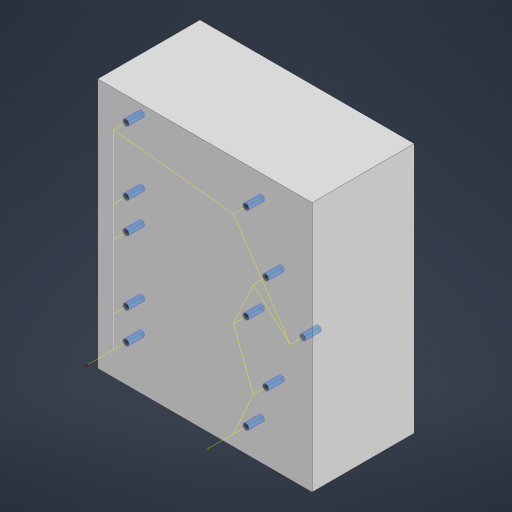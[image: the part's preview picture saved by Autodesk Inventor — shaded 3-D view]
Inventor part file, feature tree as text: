
AUTODESK INVENTOR PART (.ipt)
format: ipt  version: 2024.2 (Build 282272000, 272)  size: 536,064 bytes
history: native  units: in
note: dims shown in document units (in); Inventor stores cm internally (conversion verified against a paired STEP export)
features: other x3, sketch x2, plane x1, extrude x1, hole x1
ambient origin geometry x8: Origin, YZ Plane, XZ Plane, XY Plane, X Axis, Y Axis, Z Axis, Center Point
bodies: Solid2 (feature_tree), Solid1 (feature_tree)
feature tree (8):
  other  "HV servo drive v1_PCB.ipt"
  sketch  "Sketch1"  dims[d0=0.3937in d1=3.42in]
  plane  "Work Plane1"
  extrude  "Extrusion1"  Depth=3.42in
  hole  "Hole1"  [1 undecoded]
  other  "Solid1::HV servo drive v1_PCB.ipt"
  other  "TaggingFeature1"
  sketch  "Sketch2"  dims[d2=4.0in d3=3.47in d4=0.02in d5=0.25in d6=1.63in d7=0.0in d8=0.0849in d9=0.224in d10=0.119in d11=0.25in d12=0.5635in d13=0.28in d14=0.8108in]
note: 1 required parameter value undecoded (feature->parameter linkage not recoverable at this tier; creation-order binding heuristic only, values carry confidence <= 0.55)
